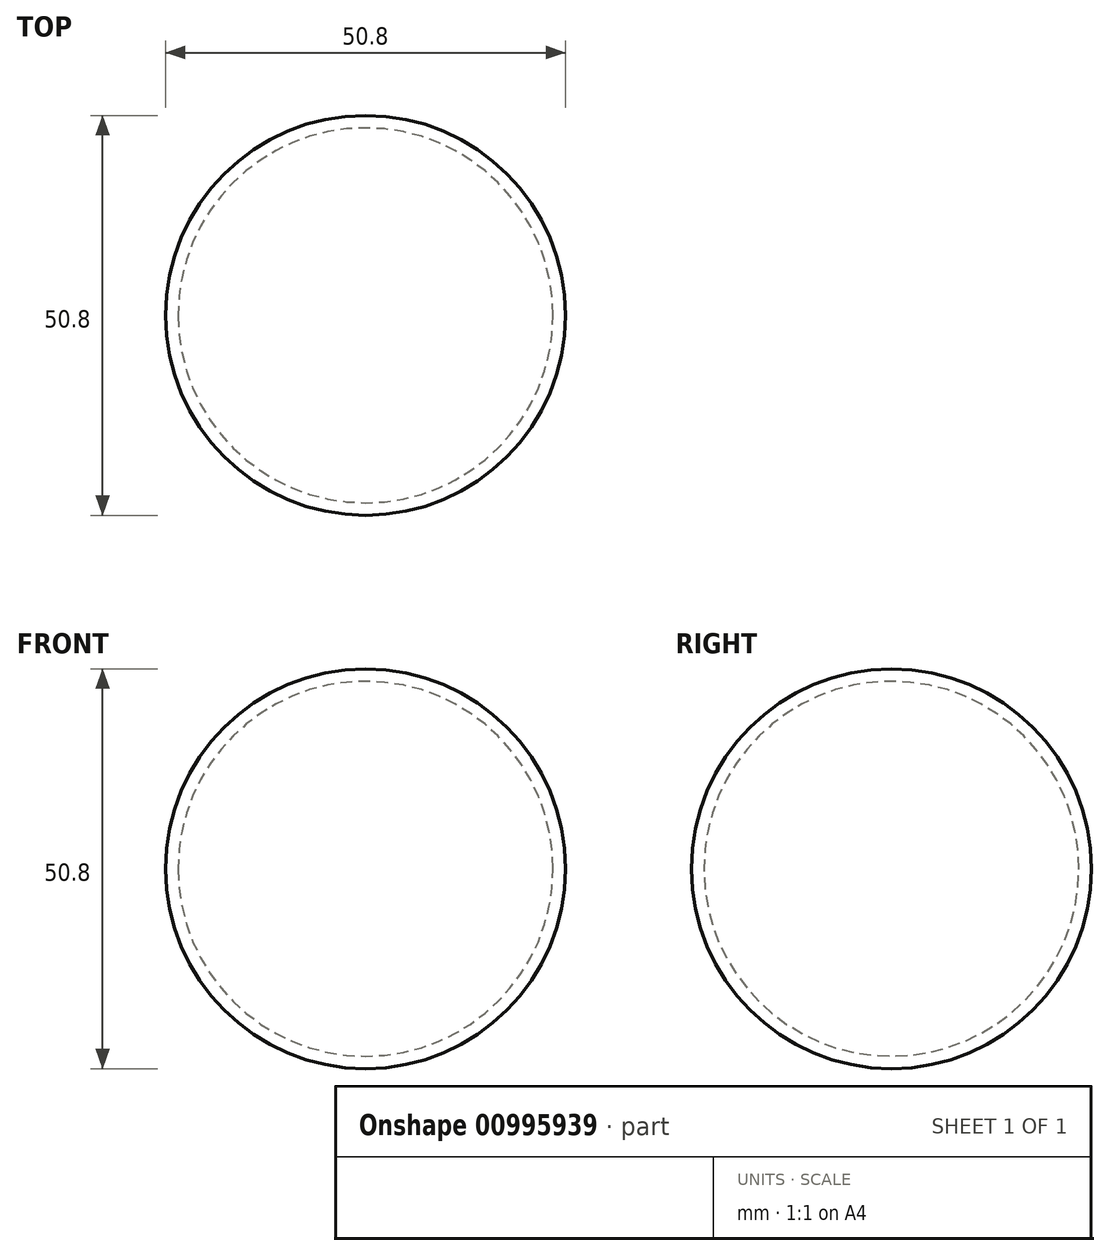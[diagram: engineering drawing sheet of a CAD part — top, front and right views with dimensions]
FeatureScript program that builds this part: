
annotation { "Feature Type Name" : "Feature", "Feature Type Description" : "" }
export const myFeature = defineFeature(function(context is Context, id is Id, definition is map)
    precondition{}
    {
        {
            var Q0;
            Q0=qCreatedBy(makeId("Top.planeOp"),FACE);
            var sketch = newSketch(context, id + "F0", { "sketchPlane" : qUnion([Q0])});
            skArc(sketch, "E0", {"start": v(25.4, 0) * mm, "mid": v(0, 25.4) * mm, "end": v(-25.4, 0) * mm});
            skArc(sketch, "E1", {"start": v(23.81, 0) * mm, "mid": v(0, 23.81) * mm, "end": v(-23.81, 0) * mm});
            skLineSegment(sketch, "E2", {"start": v(-25.4, 0) * mm, "end": v(-23.81, 0) * mm});
            skLineSegment(sketch, "E3", {"start": v(23.81, 0) * mm, "end": v(25.51, 0) * mm});
            skSolve(sketch);
        }
        {
            var Q0;
            Q0=qCreatedBy(makeId("Right.planeOp"),FACE);
            var sketch = newSketch(context, id + "F1", { "sketchPlane" : qUnion([Q0])});
            skCircle(sketch, "E4", {"center": v(0, 0) * mm, "radius": 23.81 * mm});
            skSolve(sketch);
        }
        {
            var Q0;
            {var subQ0=sQuery(id+"F0.wireOp",EDGE,"E0");Q0=makeQuery(id+"F0.imprint","IMPRINT",FACE,{"disambiguationData":[TD([[makeQuery(id+"F0.imprint","IMPRINT",EDGE,{"derivedFrom":subQ0}),1.0]])]});}
            var Q1;
            Q1=sQuery(id+"F1.wireOp",EDGE,"E4");
            revolve(context, id + "F2", {"surfaceOperationType" : NewSurfaceOperationType.NEW, "entities" : qUnion([Q0]), "axis" : qUnion([Q1]), "revolveType" : RevolveType.FULL});
        }
        {
            var Q0;
            Q0=makeQuery(id+"F2.opRevolve","SWEPT_FACE",FACE,{"disambiguationData":[OSD([sQuery(id+"F0.wireOp",EDGE,"E0")])]});
            shell(context, id + "F3", {"entities" : qUnion([Q0]), "thickness" : 1.59 * mm});
        }
    });
